# Revit family: UNB_Specchio_Multiproduct_BIM_IT_T3258;T3259;T3278;T3335;T3336;T3337;T3338_NEW
name_source: partatom
category: Plumbing Fixtures
revit_build: Autodesk Revit 2017 (Build: 20160225_1515(x64)
units: mm (PartAtom-declared; Revit-internal decimal feet)

## family parameters
Cut with Voids When Loaded = No
Host = Face
Part Type = Normal
Room Calculation Point = No
Round Connector Dimension = Use Diameter
Shared = No

## types (7) — shared parameters
Accessori = http://www.idealstandard.it
Autore = Ideal Standard
Brand = Ideal Standard
CodiceDiPrestazione = EN
Colore = specchio
Connessione = piombatura
Default Elevation = 1500 mm  [stored 4.92126 ft]
DescrizioneClassifcazioneUni2015 = Bathroom furniture
Finitura = specchio
Forma = rettangolare
Garanzia = garanzia del produttore
IfcEsportaCome = BATHROOM FURNITURE
InformazioniDiProdotto = http://www.idealstandard.it
InstruzioniInstallazione = http://www.idealstandard.it
LunghezzaNominale = 26 mm
Materiale = bicchiere
PartiDiRicambio = http://www.idealstandard.it
ProfonditàNominale = 26 mm
Revisione = 1
RiferimentoClassificazioneUni2015 = MIRRORS
Spazio = interno
Telefono = 800 652 290
TipoDiDato = Fisso
TipoEspotazioneIfc = IfcFurnitureType
TipologiaVaso = Altro
URL = http://www.idealstandard.it
UnitàDurata = anno
UnitàDurataGaranzia = anno
UnitàLineare = millimetro
UnitàMonetaria = €
UnitàSuperficie = millimetro
UnitàVolume = litro
Versione = 1
VersioneClassificazioneUni2015 = IfcFurnitureType
zero-valued in all types: Cost, CostoDiSostituzione

## per-type parameters (varying)
| type | AltezzaNominale | Caratteristiche | CodiceABarre | Description | LarghezzaNominale | Model | ModelloDiRiferimento | Nome | NomeOggettoBim | NumeroDiModello | PesoNetto | Riferimento |
| T3258 - 400 x 1000 mirror | 1000 mm  [stored 3.28084 ft] | SPECCHIO MID AMBIENT 40X100 52,7W 230W | 8014140447047 | SPECCHIO MID AMBIENT 40X100 52,7W 230W | 400 mm  [stored 1.31234 ft] | T3258BH | SPECCHIO MID AMBIENT 40X100 52,7W 230W | ISI_IdealStandard_Specchio_T3258 | ISI_IdealStandard_Specchio_T3258 | T3258BH | 6.03 Kg | T3258 |
| T3259 - 500 x 700 mirror | 700 mm  [stored 2.29659 ft] | SPECCHIO MID AMBIENT 50X70 27,8W 230W | 8014140447054 | SPECCHIO MID AMBIENT 50X70 27,8W 230W | 500 mm  [stored 1.64042 ft] | T3259BH | SPECCHIO MID AMBIENT 50X70 27,8W 230W | ISI_IdealStandard_Specchio_T3259 | ISI_IdealStandard_Specchio_T3259 | T3259BH | 4.95 Kg | T3259 |
| T3278 - 600 x 700 mirror | 700 mm  [stored 2.29659 ft] | SPECCHIO MID AMBIENT 60X70 28,7W 230W | 8014140447269 | SPECCHIO MID AMBIENT 60X70 28,7W 230W | 600 mm | T3278BH | SPECCHIO MID AMBIENT 60X70 28,7W 230W | ISI_IdealStandard_Specchio_T3278 | ISI_IdealStandard_Specchio_T3278 | T3278BH | 5.67 Kg | T3278 |
| T3335 - 700 x 700 mirror | 700 mm  [stored 2.29659 ft] | SPECCHIO MID AMBIENT 70X70 29,7W 230W | 8014140447276 | SPECCHIO MID AMBIENT 70X70 29,7W 230W | 700 mm  [stored 2.29659 ft] | T3335BH | SPECCHIO MID AMBIENT 70X70 29,7W 230W | ISI_IdealStandard_Specchio_T3335 | ISI_IdealStandard_Specchio_T3335 | T3335BH | 6.66 Kg | T3335 |
| T3336 - 800 x 700 mirror | 700 mm  [stored 2.29659 ft] | SPECCHIO MID AMBIENT 80X70 30,6W 230W | 8014140447283 | SPECCHIO MID AMBIENT 80X70 30,6W 230W | 800 mm  [stored 2.62467 ft] | T3336BH | SPECCHIO MID AMBIENT 80X70 30,6W 230W | ISI_IdealStandard_Specchio_T3336 | ISI_IdealStandard_Specchio_T3336 | T3336BH | 7.02 Kg | T3336 |
| T3337 - 1000 x 700 mirror | 700 mm  [stored 2.29659 ft] | SPECCHIO MID AMBIENT 100X70 54,6W 230W | 8014140447290 | SPECCHIO MID AMBIENT 100X70 54,6W 230W | 1000 mm  [stored 3.28084 ft] | T3337BH | SPECCHIO MID AMBIENT 100X70 54,6W 230W | ISI_IdealStandard_Specchio_T3337 | ISI_IdealStandard_Specchio_T3337 | T3337BH | 8.64 Kg | T3337 |
| T3338 - 1200 x 700 mirror | 700 mm  [stored 2.29659 ft] | SPECCHIO MID AMBIENT 120X70 56,5W 230W | 8014140447306 | SPECCHIO MID AMBIENT 120X70 56,5W 230W | 1200 mm | T3338BH | SPECCHIO MID AMBIENT 120X70 56,5W 230W | ISI_IdealStandard_Specchio_T3338 | ISI_IdealStandard_Specchio_T3338 | T3338BH | 10.04 Kg | T3338 |

note: [stored X ft] marks values corroborated as IEEE doubles in the binary element streams (Revit-internal decimal feet)

## geometry (parser evidence)
native form markers: Sweep x1
no freeform markers — native parametric forms only
